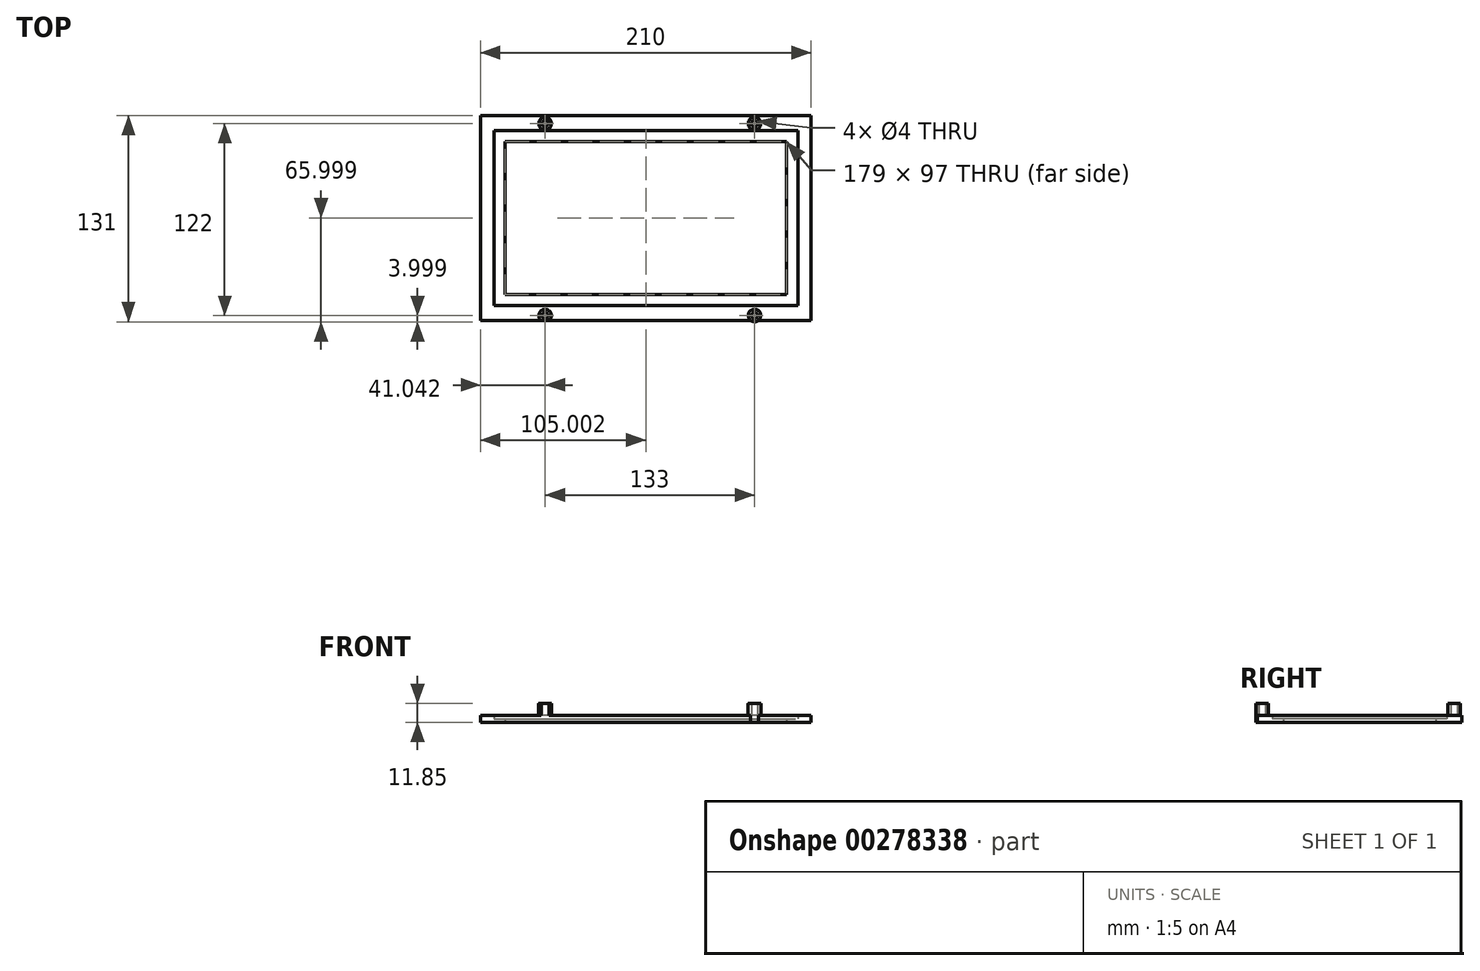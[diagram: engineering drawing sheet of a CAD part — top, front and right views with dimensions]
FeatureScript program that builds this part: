
annotation { "Feature Type Name" : "Feature", "Feature Type Description" : "" }
export const myFeature = defineFeature(function(context is Context, id is Id, definition is map)
    precondition{}
    {
        {
            var Q0;
            Q0=qCreatedBy(makeId("Top.planeOp"),FACE);
            var sketch = newSketch(context, id + "F0", { "sketchPlane" : qUnion([Q0])});
            skLineSegment(sketch, "E0.bottom", {"start": v(-66.79, 80.24) * mm, "end": v(143.21, 80.24) * mm});
            skLineSegment(sketch, "E0.top", {"start": v(-66.79, -49.76) * mm, "end": v(143.21, -49.76) * mm});
            skLineSegment(sketch, "E0.left", {"start": v(-66.79, 80.24) * mm, "end": v(-66.79, -49.76) * mm});
            skLineSegment(sketch, "E0.right", {"start": v(143.21, 80.24) * mm, "end": v(143.21, -49.76) * mm});
            skLineSegment(sketch, "E1.bottom", {"start": v(-58.29, 70.74) * mm, "end": v(134.71, 70.74) * mm});
            skLineSegment(sketch, "E1.top", {"start": v(-58.29, -40.26) * mm, "end": v(134.71, -40.26) * mm});
            skLineSegment(sketch, "E1.left", {"start": v(-58.29, 70.74) * mm, "end": v(-58.29, -40.26) * mm});
            skLineSegment(sketch, "E1.right", {"start": v(134.71, 70.74) * mm, "end": v(134.71, -40.26) * mm});
            skLineSegment(sketch, "E2.bottom", {"start": v(-51.29, 63.74) * mm, "end": v(127.71, 63.74) * mm});
            skLineSegment(sketch, "E2.top", {"start": v(-51.29, -33.26) * mm, "end": v(127.71, -33.26) * mm});
            skLineSegment(sketch, "E2.left", {"start": v(-51.29, 63.74) * mm, "end": v(-51.29, -33.26) * mm});
            skLineSegment(sketch, "E2.right", {"start": v(127.71, 63.74) * mm, "end": v(127.71, -33.26) * mm});
            skCircle(sketch, "E3", {"center": v(-25.75, 75.24) * mm, "radius": 2 * mm});
            skCircle(sketch, "E4.0.1.0", {"center": v(-25.75, -46.76) * mm, "radius": 2 * mm});
            skCircle(sketch, "E4.1.0.0", {"center": v(107.25, 75.24) * mm, "radius": 2 * mm});
            skCircle(sketch, "E4.1.1.0", {"center": v(107.25, -46.76) * mm, "radius": 2 * mm});
            skLineSegment(sketch, "E4.direction1", {"start": v(-25.75, 75.24) * mm, "end": v(107.25, 75.24) * mm, "construction": true});
            skLineSegment(sketch, "E4.direction2", {"start": v(-25.75, 75.24) * mm, "end": v(-25.75, -46.76) * mm, "construction": true});
            skCircle(sketch, "E5", {"center": v(-25.75, 75.24) * mm, "radius": 4 * mm});
            skCircle(sketch, "E6.0.1.0", {"center": v(-25.75, -46.76) * mm, "radius": 4 * mm});
            skCircle(sketch, "E6.1.0.0", {"center": v(107.25, 75.24) * mm, "radius": 4 * mm});
            skCircle(sketch, "E6.1.1.0", {"center": v(107.25, -46.76) * mm, "radius": 4 * mm});
            skSolve(sketch);
        }
        {
            var Q0;
            Q0=makeQuery(id+"F0.imprint","IMPRINT",FACE,{"disambiguationData":[TD([[makeQuery(id+"F0.imprint","IMPRINT",EDGE,{"derivedFrom":sQuery(id+"F0.wireOp",EDGE,"E1.top")}),1.0]])]});
            extrude(context, id + "F1", {"entities" : qUnion([Q0]), "depth" : 2 * mm});
        }
        {
            var Q0;
            Q0=makeQuery(id+"F0.imprint","IMPRINT",FACE,{"disambiguationData":[TD([[makeQuery(id+"F0.imprint","IMPRINT",EDGE,{"derivedFrom":sQuery(id+"F0.wireOp",EDGE,"E3")}),-1.0]])]});
            var Q1;
            Q1=makeQuery(id+"F0.imprint","IMPRINT",FACE,{"disambiguationData":[TD([[makeQuery(id+"F0.imprint","IMPRINT",EDGE,{"derivedFrom":sQuery(id+"F0.wireOp",EDGE,"E4.1.0.0")}),-1.0]])]});
            var Q2;
            Q2=makeQuery(id+"F0.imprint","IMPRINT",FACE,{"disambiguationData":[TD([[makeQuery(id+"F0.imprint","IMPRINT",EDGE,{"derivedFrom":sQuery(id+"F0.wireOp",EDGE,"E4.0.1.0")}),-1.0]])]});
            var Q3;
            Q3=makeQuery(id+"F0.imprint","IMPRINT",FACE,{"disambiguationData":[TD([[makeQuery(id+"F0.imprint","IMPRINT",EDGE,{"derivedFrom":sQuery(id+"F0.wireOp",EDGE,"E4.1.1.0")}),-1.0]])]});
            var Q4;
            Q4=makeQuery(id+"F0.imprint","IMPRINT",FACE,{"disambiguationData":[TD([[makeQuery(id+"F0.imprint","IMPRINT",EDGE,{"derivedFrom":sQuery(id+"F0.wireOp",EDGE,"E0.bottom")}),-1.0]])]});
            extrude(context, id + "F2", {"entities" : qUnion([Q0, Q1, Q2, Q3, Q4]), "operationType" : NewBodyOperationType.ADD, "depth" : 4.5 * mm});
        }
        {
            var Q0;
            Q0=makeQuery(id+"F0.imprint","IMPRINT",FACE,{"disambiguationData":[TD([[makeQuery(id+"F0.imprint","IMPRINT",EDGE,{"derivedFrom":sQuery(id+"F0.wireOp",EDGE,"E3")}),1.0]])]});
            var Q1;
            Q1=makeQuery(id+"F0.imprint","IMPRINT",FACE,{"disambiguationData":[TD([[makeQuery(id+"F0.imprint","IMPRINT",EDGE,{"derivedFrom":sQuery(id+"F0.wireOp",EDGE,"E4.1.0.0")}),1.0]])]});
            var Q2;
            Q2=makeQuery(id+"F0.imprint","IMPRINT",FACE,{"disambiguationData":[TD([[makeQuery(id+"F0.imprint","IMPRINT",EDGE,{"derivedFrom":sQuery(id+"F0.wireOp",EDGE,"E4.1.1.0")}),1.0]])]});
            var Q3;
            Q3=makeQuery(id+"F0.imprint","IMPRINT",FACE,{"disambiguationData":[TD([[makeQuery(id+"F0.imprint","IMPRINT",EDGE,{"derivedFrom":sQuery(id+"F0.wireOp",EDGE,"E4.0.1.0")}),1.0]])]});
            extrude(context, id + "F3", {"entities" : qUnion([Q0, Q1, Q2, Q3]), "operationType" : NewBodyOperationType.REMOVE, "oppositeDirection" : true, "depth" : 5 * mm});
        }
        {
            var Q0;
            Q0=makeQuery(id+"F0.imprint","IMPRINT",FACE,{"disambiguationData":[TD([[makeQuery(id+"F0.imprint","IMPRINT",EDGE,{"derivedFrom":sQuery(id+"F0.wireOp",EDGE,"E3")}),-1.0]])]});
            var Q1;
            Q1=makeQuery(id+"F0.imprint","IMPRINT",FACE,{"disambiguationData":[TD([[makeQuery(id+"F0.imprint","IMPRINT",EDGE,{"derivedFrom":sQuery(id+"F0.wireOp",EDGE,"E4.1.1.0")}),-1.0]])]});
            var Q2;
            {var subQ0=sQuery(id+"F0.wireOp",EDGE,"E6.1.1.0");var subQ1=sQuery(id+"F0.wireOp",EDGE,"E0.top");var subQ2=makeQuery(id+"F0.imprint","INTERSECT",VERTEX,{"disambiguationData":[OD(0.0)],"derivedFrom":[subQ1,subQ0]});Q2=makeQuery(id+"F0.imprint","IMPRINT",FACE,{"disambiguationData":[TD([[makeQuery(id+"F0.imprint","IMPRINT",EDGE,{"disambiguationData":[TD([[subQ2,-1.0]])],"derivedFrom":subQ1}),-1.0]])]});}
            var Q3;
            Q3=makeQuery(id+"F0.imprint","IMPRINT",FACE,{"disambiguationData":[TD([[makeQuery(id+"F0.imprint","IMPRINT",EDGE,{"derivedFrom":sQuery(id+"F0.wireOp",EDGE,"E4.0.1.0")}),-1.0]])]});
            var Q4;
            {var subQ0=sQuery(id+"F0.wireOp",EDGE,"E6.0.1.0");var subQ1=sQuery(id+"F0.wireOp",EDGE,"E0.top");var subQ2=makeQuery(id+"F0.imprint","INTERSECT",VERTEX,{"disambiguationData":[OD(0.0)],"derivedFrom":[subQ1,subQ0]});Q4=makeQuery(id+"F0.imprint","IMPRINT",FACE,{"disambiguationData":[TD([[makeQuery(id+"F0.imprint","IMPRINT",EDGE,{"disambiguationData":[TD([[subQ2,-1.0]])],"derivedFrom":subQ1}),-1.0]])]});}
            var Q5;
            Q5=makeQuery(id+"F0.imprint","IMPRINT",FACE,{"disambiguationData":[TD([[makeQuery(id+"F0.imprint","IMPRINT",EDGE,{"derivedFrom":sQuery(id+"F0.wireOp",EDGE,"E4.1.0.0")}),-1.0]])]});
            extrude(context, id + "F4", {"entities" : qUnion([Q0, Q1, Q2, Q3, Q4, Q5]), "operationType" : NewBodyOperationType.ADD, "depth" : 11.85 * mm});
        }
    });
